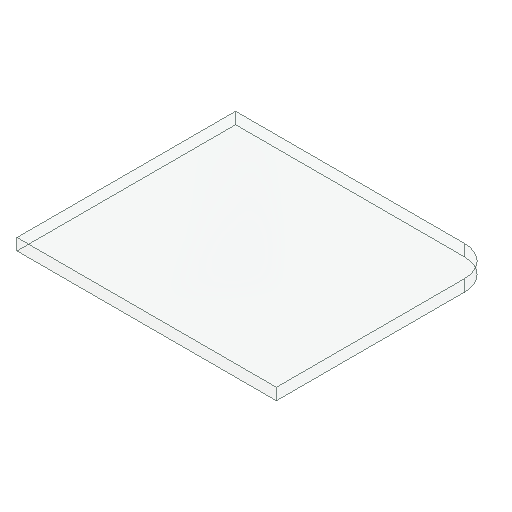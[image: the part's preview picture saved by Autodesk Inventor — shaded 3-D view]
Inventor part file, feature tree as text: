
AUTODESK INVENTOR PART (.ipt)
format: ipt  version: 2025 (Build 290162000, 162)  size: 106,496 bytes
history: native  units: mm
features: reference x5, extrude x2, sketch x2, other x2
ambient origin geometry x8: Origin, YZ Plane, XZ Plane, XY Plane, X Axis, Y Axis, Z Axis, Center Point
bodies: Solid1 (feature_tree)
feature tree (11):
  extrude  "Extrusion1"  Depth=40.0mm
  extrude  "Extrusion2"  Depth=10.0mm
  sketch  "Sketch1"  dims[d0=50.0mm d1=40.0mm]
  sketch  "Sketch2"  dims[d2=2.0mm d3=0.0mm d5=0.25mm d6=10.0mm d7=0.0mm d8=8.0mm]
  reference  "Reference1"
  reference  "Reference2"
  reference  "Reference3"
  reference  "Reference4"
  reference  "Reference5"
  other  "USB_C_PD_PPS_sink_with_enclosure.iam"
  other  "top_enclosure:1"
